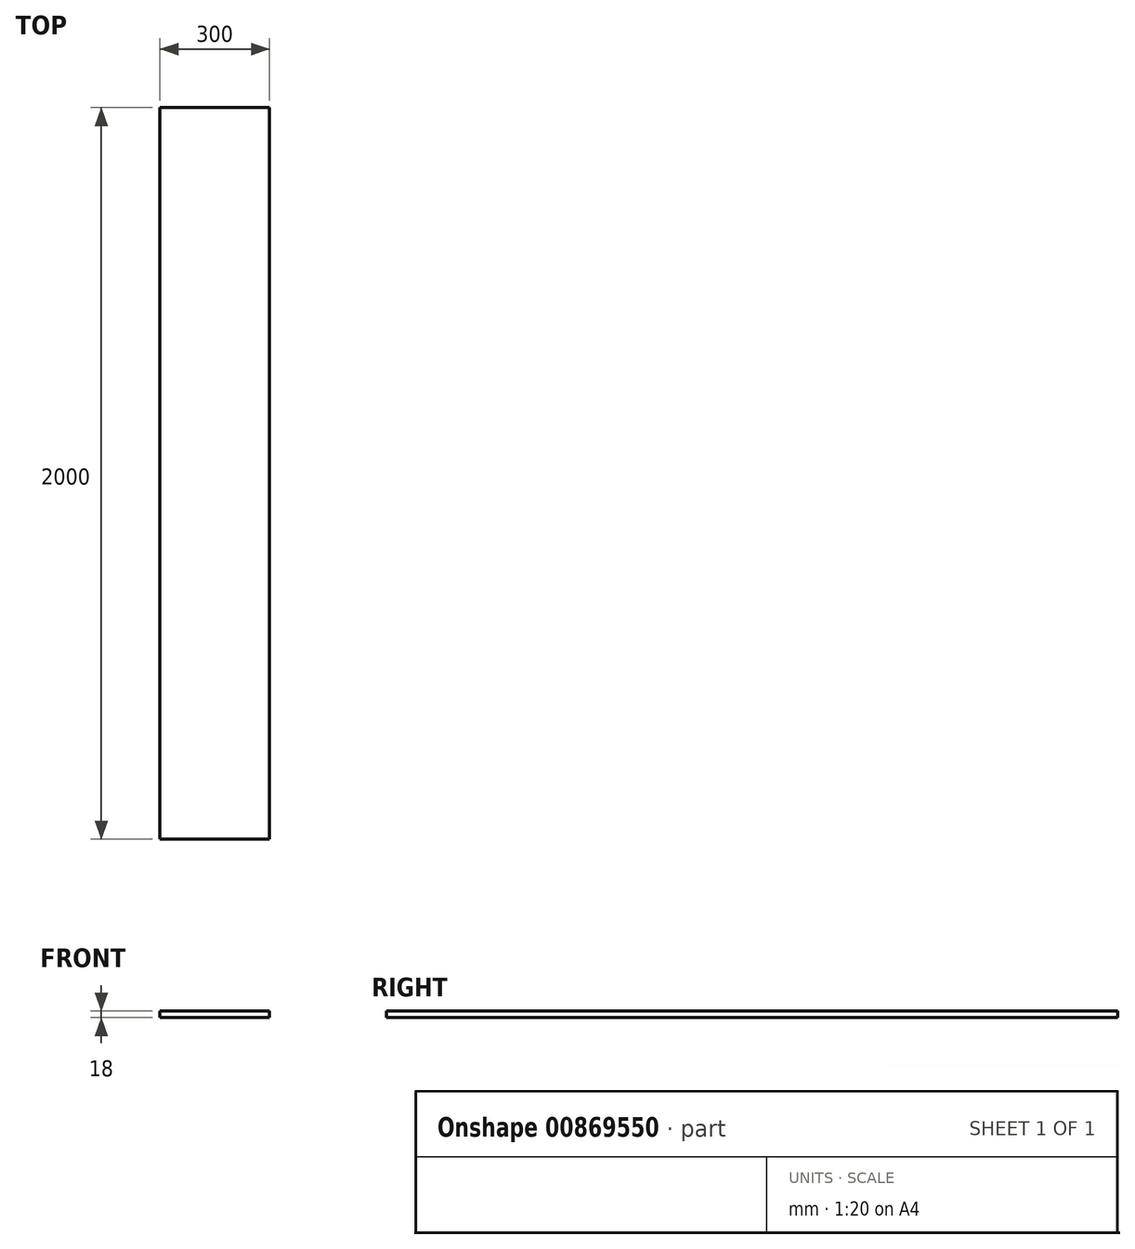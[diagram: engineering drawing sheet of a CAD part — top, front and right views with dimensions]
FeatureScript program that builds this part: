
annotation { "Feature Type Name" : "Feature", "Feature Type Description" : "" }
export const myFeature = defineFeature(function(context is Context, id is Id, definition is map)
    precondition{}
    {
        {
            var Q0;
            Q0=qCreatedBy(makeId("Top.planeOp"),FACE);
            var sketch = newSketch(context, id + "F0", { "sketchPlane" : qUnion([Q0])});
            skLineSegment(sketch, "E0.bottom", {"start": v(0, 0) * mm, "end": v(300, 0) * mm});
            skLineSegment(sketch, "E0.top", {"start": v(0, 2000) * mm, "end": v(300, 2000) * mm});
            skLineSegment(sketch, "E0.left", {"start": v(0, 0) * mm, "end": v(0, 2000) * mm});
            skLineSegment(sketch, "E0.right", {"start": v(300, 0) * mm, "end": v(300, 2000) * mm});
            skSolve(sketch);
        }
        {
            var Q0;
            Q0 = qSketchRegion(id + "F0", true);
            extrude(context, id + "F1", {"entities" : qUnion([Q0]), "depth" : 18 * mm, "offsetDistance" : 25 * mm});
        }
    });
